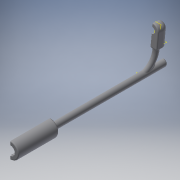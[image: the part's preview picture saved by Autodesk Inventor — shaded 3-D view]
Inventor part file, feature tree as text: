
AUTODESK INVENTOR PART (.ipt)
format: ipt  version: 2018 (Build 220112000, 112)  size: 443,392 bytes
history: native  units: mm
features: sketch x10, extrude x8, fillet x6, plane x3, projected_geometry x3, revolve x1, sweep x1
ambient origin geometry x8: Origin, YZ Plane, XZ Plane, XY Plane, X Axis, Y Axis, Z Axis, Center Point
bodies: Solid1 (feature_tree)
feature tree (32):
  revolve  "Revolution1"  [1 undecoded]
  fillet  "Fillet1"  Radius=8.0mm
  fillet  "Fillet2"  Radius=40.0mm
  fillet  "Fillet3"  [1 undecoded]
  plane  "Work Plane1"
  sweep  "Sweep1"
  extrude  "Extrusion2"  Depth=1.0mm
  fillet  "Fillet4"  Radius=1.0mm
  fillet  "Fillet5"  Radius=1.0mm
  extrude  "Extrusion3"  Depth=4.0mm
  extrude  "Extrusion4"  Depth=2.0mm
  extrude  "Extrusion5"  Depth=1.0mm
  extrude  "Extrusion6"  Depth=18.0mm
  extrude  "Extrusion7"  Depth=16.0mm
  plane  "Work Plane3"
  extrude  "Extrusion8"  Depth=12.0mm
  plane  "Work Plane5"
  extrude  "Extrusion9"  Depth=6.0mm
  fillet  "Fillet6"  Radius=6.0mm
  sketch  "Sketch6"  dims[d0=150.0mm d1=3.5mm d3=8.0mm d4=40.0mm d5=90.0deg]
  sketch  "Sketch8"  dims[d20=1.5mm d21=1.5mm]
  sketch  "Sketch9"  dims[d22=1.5mm d23=1.0mm d24=1.0mm d25=1.0mm]
  projected_geometry  "Projected Loop3"
  sketch  "Sketch10"  dims[d26=1.5mm d27=4.0mm]
  projected_geometry  "Projected Loop4"
  sketch  "Sketch11"  dims[d29=9.0mm d30=2.0mm]
  sketch  "Sketch12"  dims[d31=1.0mm d32=1.0mm]
  sketch  "Sketch13"  dims[d33=-23.0mm d38=18.0mm]
  sketch  "Sketch14"  dims[d39=18.0mm d40=16.0mm]
  sketch  "Sketch15"  dims[d41=0.0mm d42=0.0mm d43=12.0mm]
  projected_geometry  "Projected Loop5"
  sketch  "Sketch16"  dims[d44=5.0mm d45=6.0mm d46=6.0mm d47=20.0mm d48=0.0mm d49=6.0mm d50=1.0mm d51=4.0mm d52=5.5mm d53=8.0mm d54=0.0mm d55=10.0mm d56=0.0mm d57=50.0mm d58=0.0mm d59=1.4mm d60=0.0mm d62=15.0mm d63=0.0mm d64=-3.0mm d65=6.5mm d66=1.1mm d67=0.0mm d68=-3.0mm d69=10.0mm d70=0.0mm d71=0.5mm d72=6.0mm d73=8.25mm d74=8.25mm d75=0.0mm]
note: 2 required parameter values undecoded (feature->parameter linkage not recoverable at this tier; creation-order binding heuristic only, values carry confidence <= 0.55)